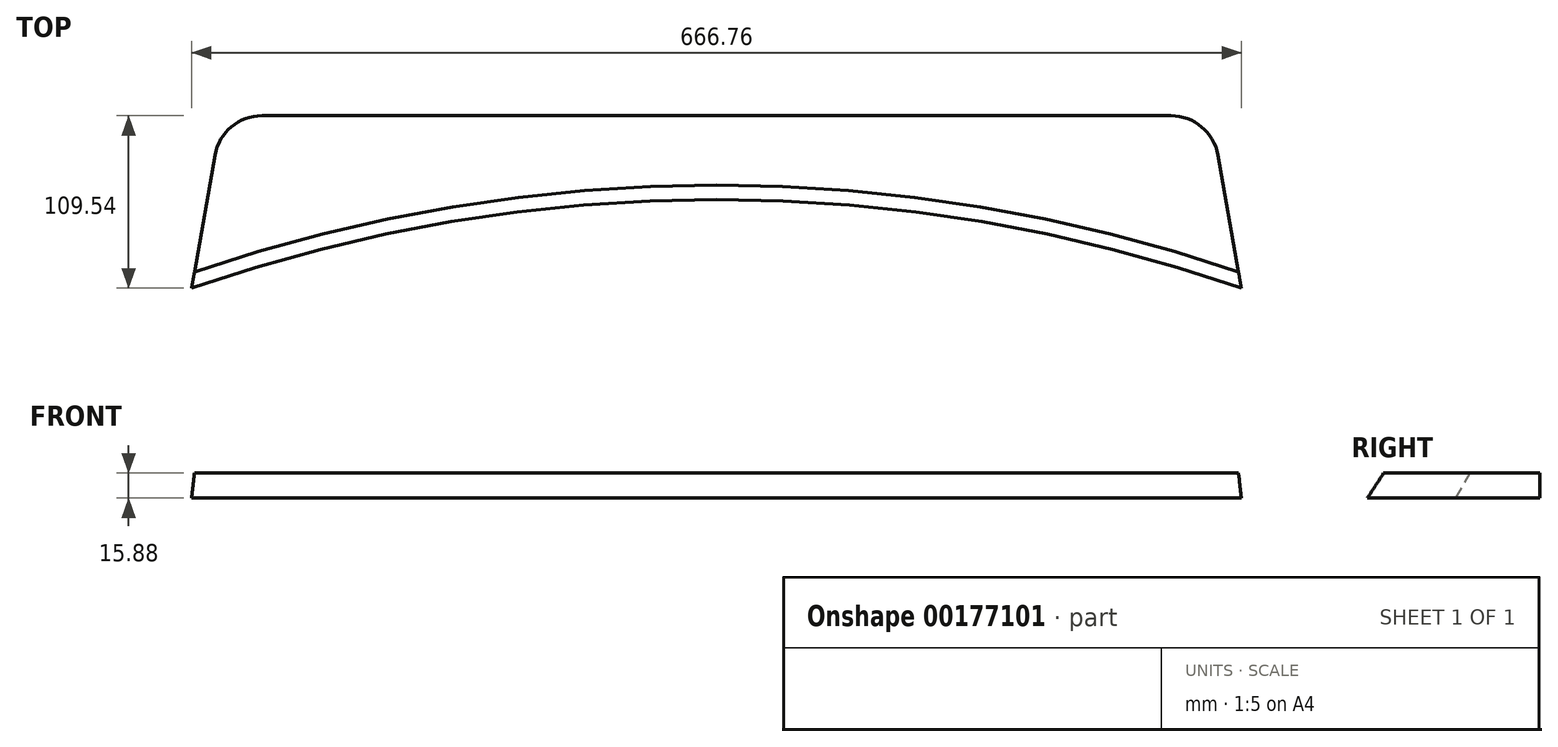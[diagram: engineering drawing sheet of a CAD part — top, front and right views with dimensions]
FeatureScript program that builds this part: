
annotation { "Feature Type Name" : "Feature", "Feature Type Description" : "" }
export const myFeature = defineFeature(function(context is Context, id is Id, definition is map)
    precondition{}
    {
        {
            var Q0;
            Q0=qCreatedBy(makeId("Top.planeOp"),FACE);
            var sketch = newSketch(context, id + "F0", { "sketchPlane" : qUnion([Q0])});
            skLineSegment(sketch, "E0", {"start": v(-333.38, 0) * mm, "end": v(333.38, 0) * mm, "construction": true});
            skArc(sketch, "E1", {"start": v(333.38, 0) * mm, "mid": v(0, 56.25) * mm, "end": v(-333.38, 0) * mm});
            skLineSegment(sketch, "E2", {"start": v(-333.38, 0) * mm, "end": v(-318.46, 84.61) * mm});
            skArc(sketch, "E3", {"start": v(-288.75, 109.54) * mm, "mid": v(-308.14, 102.48) * mm, "end": v(-318.46, 84.61) * mm});
            skLineSegment(sketch, "E4", {"start": v(-288.75, 109.54) * mm, "end": v(288.75, 109.54) * mm});
            skArc(sketch, "E5", {"start": v(318.46, 84.61) * mm, "mid": v(308.14, 102.48) * mm, "end": v(288.75, 109.54) * mm});
            skLineSegment(sketch, "E6", {"start": v(333.38, 0) * mm, "end": v(318.46, 84.61) * mm});
            skLineSegment(sketch, "E7", {"start": v(0, 0) * mm, "end": v(0, 109.54) * mm, "construction": true});
            skPoint(sketch, "E7.endSnap0", {"position": v(0, 109.54) * mm});
            skSolve(sketch);
        }
        {
            var Q0;
            Q0=makeQuery(id+"F0.imprint","IMPRINT",FACE,{"disambiguationData":[TD([[makeQuery(id+"F0.imprint","IMPRINT",EDGE,{"derivedFrom":sQuery(id+"F0.wireOp",EDGE,"E1")}),-1.0]])]});
            extrude(context, id + "F1", {"entities" : qUnion([Q0]), "depth" : 15.88 * mm});
        }
        {
            var Q0;
            Q0=makeQuery(id+"F1.opExtrude","CAP_EDGE",EDGE,{"disambiguationData":[OSD([sQuery(id+"F0.wireOp",EDGE,"E1")])],"isStart":false});
            chamfer(context, id + "F2", {"entities" : qUnion([Q0]), "chamferType" : ChamferType.OFFSET_ANGLE, "width" : 15.88 * mm, "oppositeDirection" : false, "angle" : 30 * degree, "tangentPropagation" : true});
        }
    });
